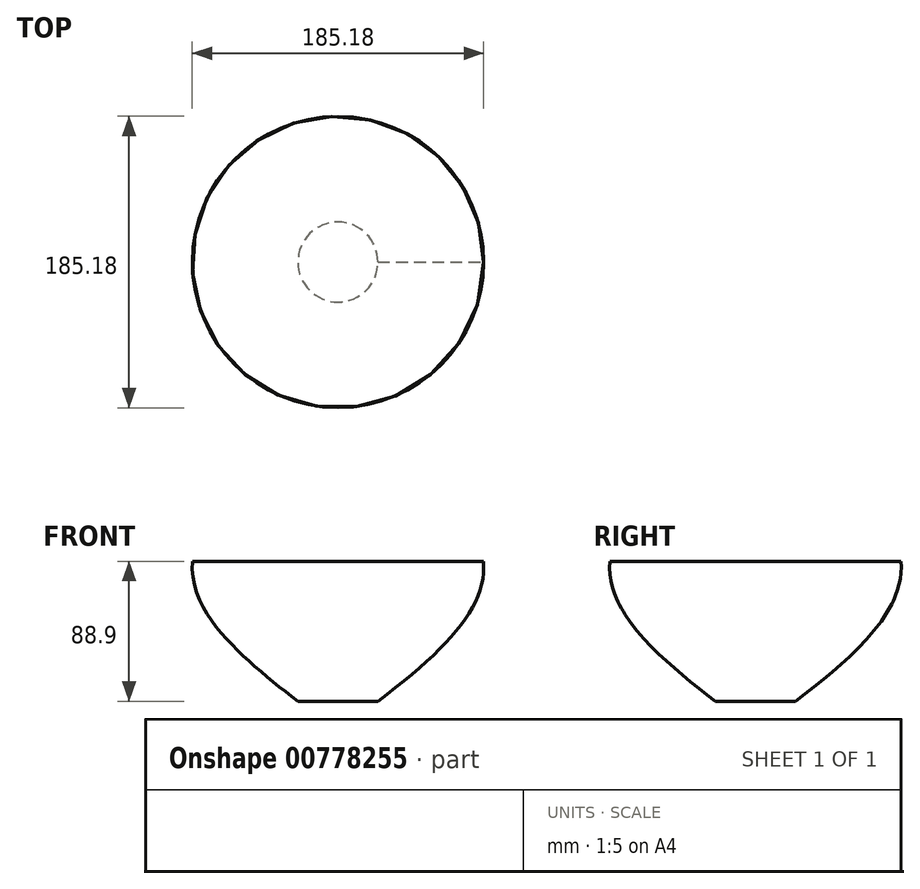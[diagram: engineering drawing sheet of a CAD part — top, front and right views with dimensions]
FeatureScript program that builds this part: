
annotation { "Feature Type Name" : "Feature", "Feature Type Description" : "" }
export const myFeature = defineFeature(function(context is Context, id is Id, definition is map)
    precondition{}
    {
        {
            var Q0;
            Q0=qCreatedBy(makeId("Front.planeOp"),FACE);
            var sketch = newSketch(context, id + "F0", { "sketchPlane" : qUnion([Q0])});
            skLineSegment(sketch, "E0", {"start": v(0, 0) * mm, "end": v(25.4, 0) * mm});
            skLineSegment(sketch, "E1", {"start": v(0, 88.9) * mm, "end": v(92.46, 88.9) * mm});
            skPoint(sketch, "E2.center.orphan", {"position": v(0, 88.9) * mm});
            skPoint(sketch, "E3.start.orphan", {"position": v(-126.23, 88.9) * mm});
            skLineSegment(sketch, "E4", {"start": v(0, 88.9) * mm, "end": v(0, 0) * mm});
            skLineSegment(sketch, "E5", {"start": v(0, 0) * mm, "end": v(0, -17.31) * mm, "construction": true});
            skFitSpline(sketch, "E6", {"points": [v(25.4, 0) * mm, v(92.46, 88.9) * mm], "startDerivative": vector(135.13, 102.12) * mm, "endDerivative": vector(-6.37, 86.02) * mm});
            skSolve(sketch);
        }
        {
            var Q0;
            Q0 = qSketchRegion(id + "F0", true);
            var Q1;
            Q1=sQuery(id+"F0.wireOp",EDGE,"E5");
            revolve(context, id + "F1", {"surfaceOperationType" : NewSurfaceOperationType.NEW, "entities" : qUnion([Q0]), "axis" : qUnion([Q1]), "revolveType" : RevolveType.FULL});
        }
    });
